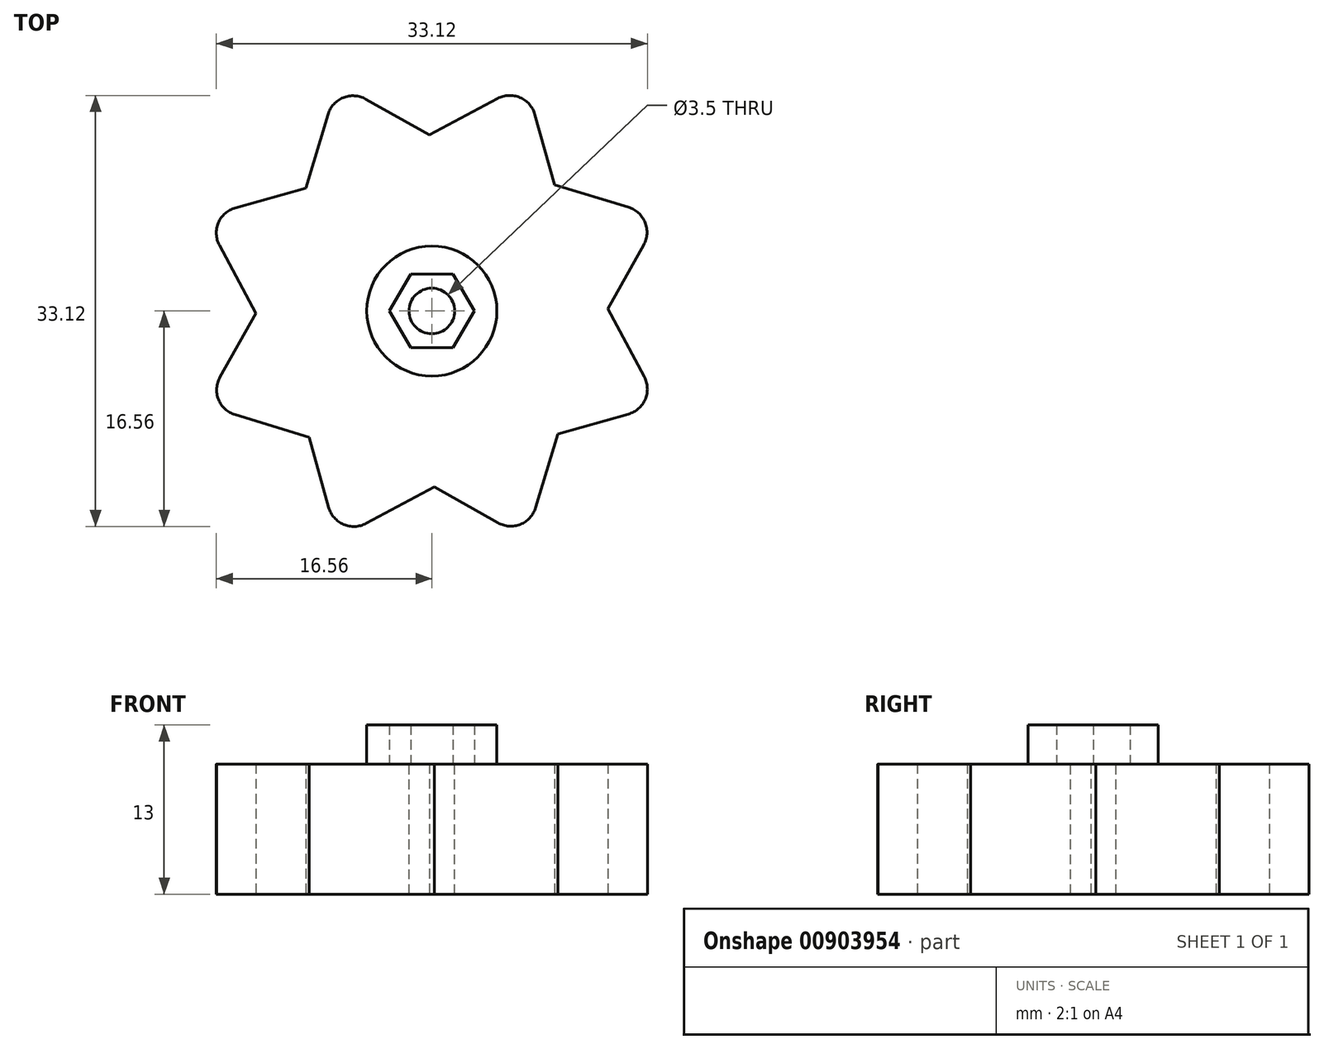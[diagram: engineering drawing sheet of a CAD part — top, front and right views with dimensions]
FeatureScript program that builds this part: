
annotation { "Feature Type Name" : "Feature", "Feature Type Description" : "" }
export const myFeature = defineFeature(function(context is Context, id is Id, definition is map)
    precondition{}
    {
        {
            var Q0;
            Q0=qCreatedBy(makeId("Top.planeOp"),FACE);
            var sketch = newSketch(context, id + "F0", { "sketchPlane" : qUnion([Q0])});
            skPoint(sketch, "E0.0.midPoint", {"position": v(-4.94, 11.48) * mm});
            skLineSegment(sketch, "E1", {"start": v(-9.7, 9.44) * mm, "end": v(-7.97, 15.12) * mm});
            skLineSegment(sketch, "E2", {"start": v(-0.18, 13.53) * mm, "end": v(-5.08, 16.28) * mm});
            skLineSegment(sketch, "E3", {"start": v(-0.18, 13.53) * mm, "end": v(5.05, 16.33) * mm});
            skLineSegment(sketch, "E4", {"start": v(7.92, 15.1) * mm, "end": v(9.44, 9.7) * mm});
            skLineSegment(sketch, "E5", {"start": v(9.44, 9.7) * mm, "end": v(15.12, 7.97) * mm});
            skLineSegment(sketch, "E6", {"start": v(16.28, 5.08) * mm, "end": v(13.53, 0.18) * mm});
            skLineSegment(sketch, "E7", {"start": v(16.33, -5.05) * mm, "end": v(13.53, 0.18) * mm});
            skLineSegment(sketch, "E8", {"start": v(15.1, -7.92) * mm, "end": v(9.7, -9.44) * mm});
            skLineSegment(sketch, "E9", {"start": v(9.7, -9.44) * mm, "end": v(7.97, -15.12) * mm});
            skLineSegment(sketch, "E10", {"start": v(5.08, -16.28) * mm, "end": v(0.18, -13.53) * mm});
            skLineSegment(sketch, "E11", {"start": v(0.18, -13.53) * mm, "end": v(-5.05, -16.33) * mm});
            skLineSegment(sketch, "E12", {"start": v(-7.92, -15.1) * mm, "end": v(-9.44, -9.7) * mm});
            skLineSegment(sketch, "E13", {"start": v(-9.44, -9.7) * mm, "end": v(-15.12, -7.97) * mm});
            skLineSegment(sketch, "E14", {"start": v(-16.28, -5.08) * mm, "end": v(-13.53, -0.18) * mm});
            skLineSegment(sketch, "E15", {"start": v(-13.53, -0.18) * mm, "end": v(-16.33, 5.05) * mm});
            skLineSegment(sketch, "E16", {"start": v(-15.1, 7.92) * mm, "end": v(-9.7, 9.44) * mm});
            skPoint(sketch, "E17.visualSharp", {"position": v(-17.5, 7.25) * mm});
            skArc(sketch, "E17.filletArc", {"start": v(-15.1, 7.92) * mm, "mid": v(-16.4, 6.78) * mm, "end": v(-16.33, 5.05) * mm});
            skPoint(sketch, "E18.visualSharp", {"position": v(-7.25, 17.5) * mm});
            skArc(sketch, "E18.filletArc", {"start": v(-5.08, 16.28) * mm, "mid": v(-6.8, 16.4) * mm, "end": v(-7.97, 15.12) * mm});
            skPoint(sketch, "E19.visualSharp", {"position": v(7.25, 17.5) * mm});
            skArc(sketch, "E19.filletArc", {"start": v(7.92, 15.1) * mm, "mid": v(6.78, 16.4) * mm, "end": v(5.05, 16.33) * mm});
            skPoint(sketch, "E20.visualSharp", {"position": v(17.5, 7.25) * mm});
            skArc(sketch, "E20.filletArc", {"start": v(16.28, 5.08) * mm, "mid": v(16.4, 6.8) * mm, "end": v(15.12, 7.97) * mm});
            skPoint(sketch, "E21.visualSharp", {"position": v(17.5, -7.25) * mm});
            skArc(sketch, "E21.filletArc", {"start": v(15.1, -7.92) * mm, "mid": v(16.4, -6.78) * mm, "end": v(16.33, -5.05) * mm});
            skPoint(sketch, "E22.visualSharp", {"position": v(7.25, -17.5) * mm});
            skArc(sketch, "E22.filletArc", {"start": v(5.08, -16.28) * mm, "mid": v(6.8, -16.4) * mm, "end": v(7.97, -15.12) * mm});
            skPoint(sketch, "E23.visualSharp", {"position": v(-7.25, -17.5) * mm});
            skArc(sketch, "E23.filletArc", {"start": v(-7.92, -15.1) * mm, "mid": v(-6.78, -16.4) * mm, "end": v(-5.05, -16.33) * mm});
            skPoint(sketch, "E24.visualSharp", {"position": v(-17.5, -7.25) * mm});
            skArc(sketch, "E24.filletArc", {"start": v(-16.28, -5.08) * mm, "mid": v(-16.4, -6.8) * mm, "end": v(-15.12, -7.97) * mm});
            skSolve(sketch);
        }
        {
            var Q0;
            Q0 = qSketchRegion(id + "F0", true);
            extrude(context, id + "F1", {"entities" : qUnion([Q0]), "depth" : 10 * mm, "offsetDistance" : 25 * mm});
        }
        {
            var Q0;
            Q0=makeQuery(id+"F1.opExtrude","CAP_FACE",FACE,{"disambiguationData":[OSD([sQuery(id+"F0.wireOp",EDGE,"E1"),sQuery(id+"F0.wireOp",EDGE,"E2"),sQuery(id+"F0.wireOp",EDGE,"E3"),sQuery(id+"F0.wireOp",EDGE,"E4"),sQuery(id+"F0.wireOp",EDGE,"E5"),sQuery(id+"F0.wireOp",EDGE,"E6"),sQuery(id+"F0.wireOp",EDGE,"E7"),sQuery(id+"F0.wireOp",EDGE,"E8"),sQuery(id+"F0.wireOp",EDGE,"E9"),sQuery(id+"F0.wireOp",EDGE,"E10"),sQuery(id+"F0.wireOp",EDGE,"E11"),sQuery(id+"F0.wireOp",EDGE,"E12"),sQuery(id+"F0.wireOp",EDGE,"E13"),sQuery(id+"F0.wireOp",EDGE,"E14"),sQuery(id+"F0.wireOp",EDGE,"E15"),sQuery(id+"F0.wireOp",EDGE,"E16"),sQuery(id+"F0.wireOp",EDGE,"E17.filletArc"),sQuery(id+"F0.wireOp",EDGE,"E18.filletArc"),sQuery(id+"F0.wireOp",EDGE,"E19.filletArc"),sQuery(id+"F0.wireOp",EDGE,"E20.filletArc"),sQuery(id+"F0.wireOp",EDGE,"E21.filletArc"),sQuery(id+"F0.wireOp",EDGE,"E22.filletArc"),sQuery(id+"F0.wireOp",EDGE,"E23.filletArc"),sQuery(id+"F0.wireOp",EDGE,"E24.filletArc")])],"isStart":false});
            var sketch = newSketch(context, id + "F2", { "sketchPlane" : qUnion([Q0])});
            skCircle(sketch, "E25", {"center": v(0, 0) * mm, "radius": 5 * mm});
            skCircle(sketch, "E26.cCircle", {"center": v(0, 0) * mm, "radius": 2.83 * mm, "construction": true});
            skLineSegment(sketch, "E26.0", {"start": v(-1.63, 2.83) * mm, "end": v(1.63, 2.83) * mm});
            skLineSegment(sketch, "E26.1", {"start": v(1.63, 2.83) * mm, "end": v(3.26, 0) * mm});
            skLineSegment(sketch, "E26.2", {"start": v(3.26, 0) * mm, "end": v(1.63, -2.83) * mm});
            skLineSegment(sketch, "E26.3", {"start": v(1.63, -2.82) * mm, "end": v(-1.63, -2.83) * mm});
            skLineSegment(sketch, "E26.4", {"start": v(-1.63, -2.83) * mm, "end": v(-3.26, 0) * mm});
            skLineSegment(sketch, "E26.5", {"start": v(-3.26, 0) * mm, "end": v(-1.63, 2.83) * mm});
            skPoint(sketch, "E26.0.midPoint", {"position": v(0, 2.83) * mm});
            skSolve(sketch);
        }
        {
            var Q0;
            Q0=makeQuery(id+"F2.imprint","IMPRINT",FACE,{"disambiguationData":[TD([[makeQuery(id+"F2.imprint","IMPRINT",EDGE,{"derivedFrom":sQuery(id+"F2.wireOp",EDGE,"E25")}),1.0]])]});
            extrude(context, id + "F3", {"entities" : qUnion([Q0]), "operationType" : NewBodyOperationType.ADD, "depth" : 3 * mm, "offsetDistance" : 25 * mm});
        }
        {
            var Q0;
            Q0=makeQuery(id+"F3.boolean.opBoolean","SPLIT",FACE,{"disambiguationData":[TD([makeQuery(id+"F3.opExtrude","SWEPT_FACE",FACE,{"disambiguationData":[OSD([sQuery(id+"F2.wireOp",EDGE,"E26.0")])]})])],"derivedFrom":makeQuery(id+"F1.opExtrude","CAP_FACE",FACE,{"disambiguationData":[OSD([sQuery(id+"F0.wireOp",EDGE,"E1"),sQuery(id+"F0.wireOp",EDGE,"E2"),sQuery(id+"F0.wireOp",EDGE,"E3"),sQuery(id+"F0.wireOp",EDGE,"E4"),sQuery(id+"F0.wireOp",EDGE,"E5"),sQuery(id+"F0.wireOp",EDGE,"E6"),sQuery(id+"F0.wireOp",EDGE,"E7"),sQuery(id+"F0.wireOp",EDGE,"E8"),sQuery(id+"F0.wireOp",EDGE,"E9"),sQuery(id+"F0.wireOp",EDGE,"E10"),sQuery(id+"F0.wireOp",EDGE,"E11"),sQuery(id+"F0.wireOp",EDGE,"E12"),sQuery(id+"F0.wireOp",EDGE,"E13"),sQuery(id+"F0.wireOp",EDGE,"E14"),sQuery(id+"F0.wireOp",EDGE,"E15"),sQuery(id+"F0.wireOp",EDGE,"E16"),sQuery(id+"F0.wireOp",EDGE,"E17.filletArc"),sQuery(id+"F0.wireOp",EDGE,"E18.filletArc"),sQuery(id+"F0.wireOp",EDGE,"E19.filletArc"),sQuery(id+"F0.wireOp",EDGE,"E20.filletArc"),sQuery(id+"F0.wireOp",EDGE,"E21.filletArc"),sQuery(id+"F0.wireOp",EDGE,"E22.filletArc"),sQuery(id+"F0.wireOp",EDGE,"E23.filletArc"),sQuery(id+"F0.wireOp",EDGE,"E24.filletArc")])],"isStart":false})});
            var sketch = newSketch(context, id + "F4", { "sketchPlane" : qUnion([Q0])});
            skCircle(sketch, "E27", {"center": v(0, 0) * mm, "radius": 1.75 * mm});
            skSolve(sketch);
        }
        {
            var Q0;
            Q0=makeQuery(id+"F4.imprint","IMPRINT",FACE,{"disambiguationData":[TD([[makeQuery(id+"F4.imprint","IMPRINT",EDGE,{"derivedFrom":sQuery(id+"F4.wireOp",EDGE,"E27")}),1.0]])]});
            extrude(context, id + "F5", {"entities" : qUnion([Q0]), "operationType" : NewBodyOperationType.REMOVE, "endBound" : BoundingType.THROUGH_ALL, "oppositeDirection" : true, "depth" : 25 * mm, "offsetDistance" : 25 * mm});
        }
    });
